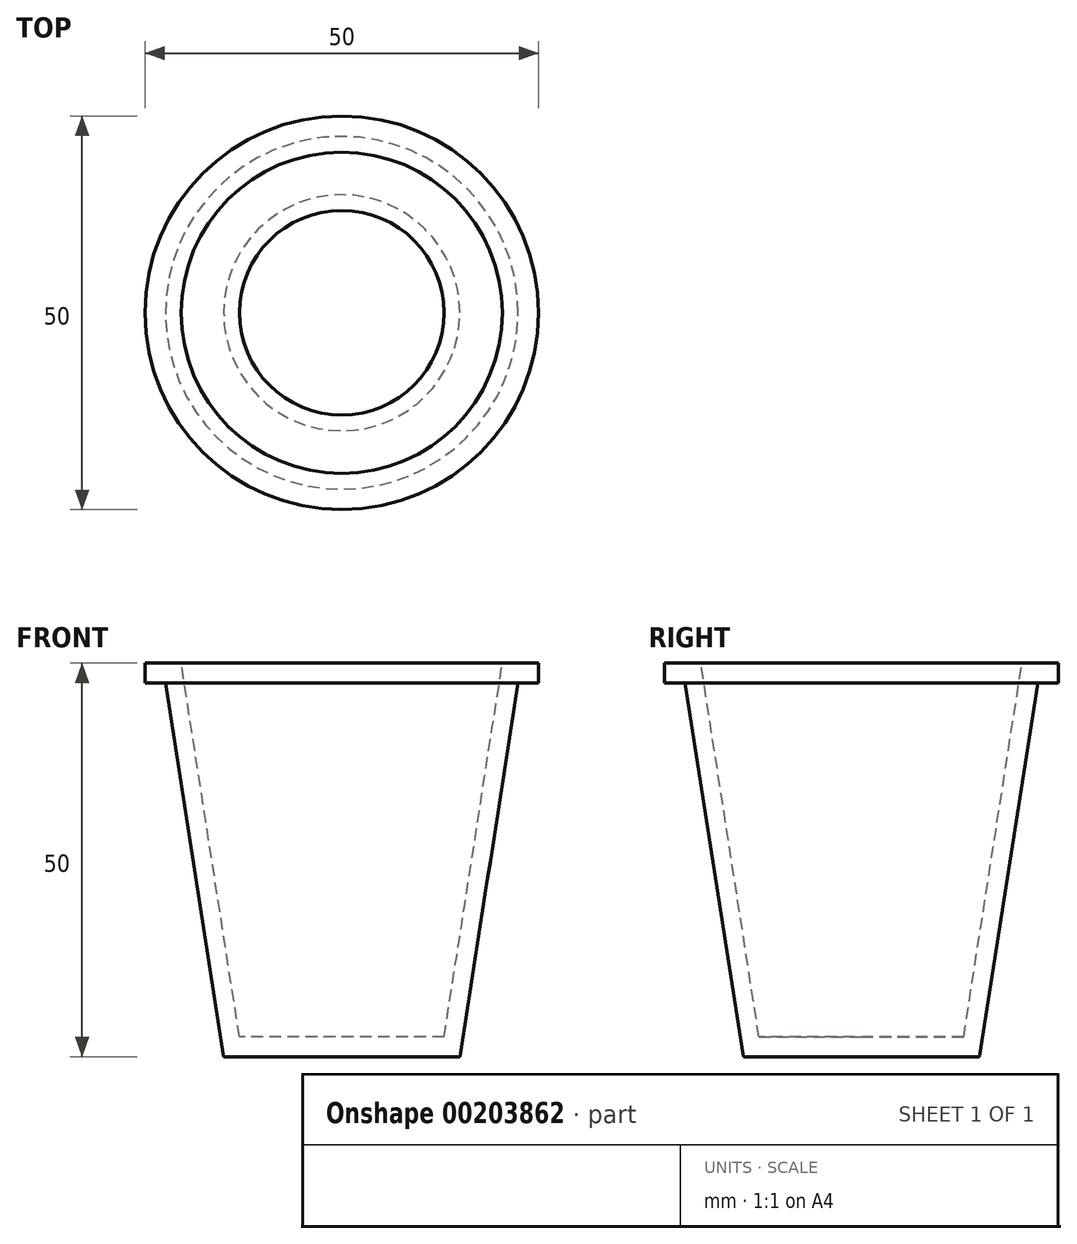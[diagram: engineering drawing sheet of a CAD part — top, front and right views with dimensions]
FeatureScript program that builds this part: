
annotation { "Feature Type Name" : "Feature", "Feature Type Description" : "" }
export const myFeature = defineFeature(function(context is Context, id is Id, definition is map)
    precondition{}
    {
        {
            var Q0;
            Q0=qCreatedBy(makeId("Front.planeOp"),FACE);
            var sketch = newSketch(context, id + "F0", { "sketchPlane" : qUnion([Q0])});
            skLineSegment(sketch, "E0", {"start": v(0, 0) * mm, "end": v(15, 0) * mm});
            skLineSegment(sketch, "E1", {"start": v(15, 0) * mm, "end": v(22.4, 47.5) * mm});
            skLineSegment(sketch, "E2", {"start": v(22.4, 47.5) * mm, "end": v(25, 47.5) * mm});
            skLineSegment(sketch, "E3", {"start": v(25, 47.5) * mm, "end": v(25, 50) * mm});
            skLineSegment(sketch, "E4", {"start": v(25, 50) * mm, "end": v(20.4, 50) * mm});
            skLineSegment(sketch, "E5", {"start": v(20.4, 50) * mm, "end": v(13, 2.5) * mm});
            skLineSegment(sketch, "E6", {"start": v(13, 2.5) * mm, "end": v(0, 2.5) * mm});
            skLineSegment(sketch, "E7", {"start": v(0, 2.5) * mm, "end": v(0, 0) * mm});
            skLineSegment(sketch, "E8", {"start": v(0, 54.92) * mm, "end": v(0, -61.32) * mm, "construction": true});
            skSolve(sketch);
        }
        {
            var Q0;
            Q0=makeQuery(id+"F0.imprint","IMPRINT",FACE,{"disambiguationData":[TD([[makeQuery(id+"F0.imprint","IMPRINT",EDGE,{"derivedFrom":sQuery(id+"F0.wireOp",EDGE,"E0")}),1.0]])]});
            var Q1;
            Q1=sQuery(id+"F0.wireOp",EDGE,"E8");
            revolve(context, id + "F1", {"entities" : qUnion([Q0]), "axis" : qUnion([Q1]), "revolveType" : RevolveType.FULL});
        }
    });
